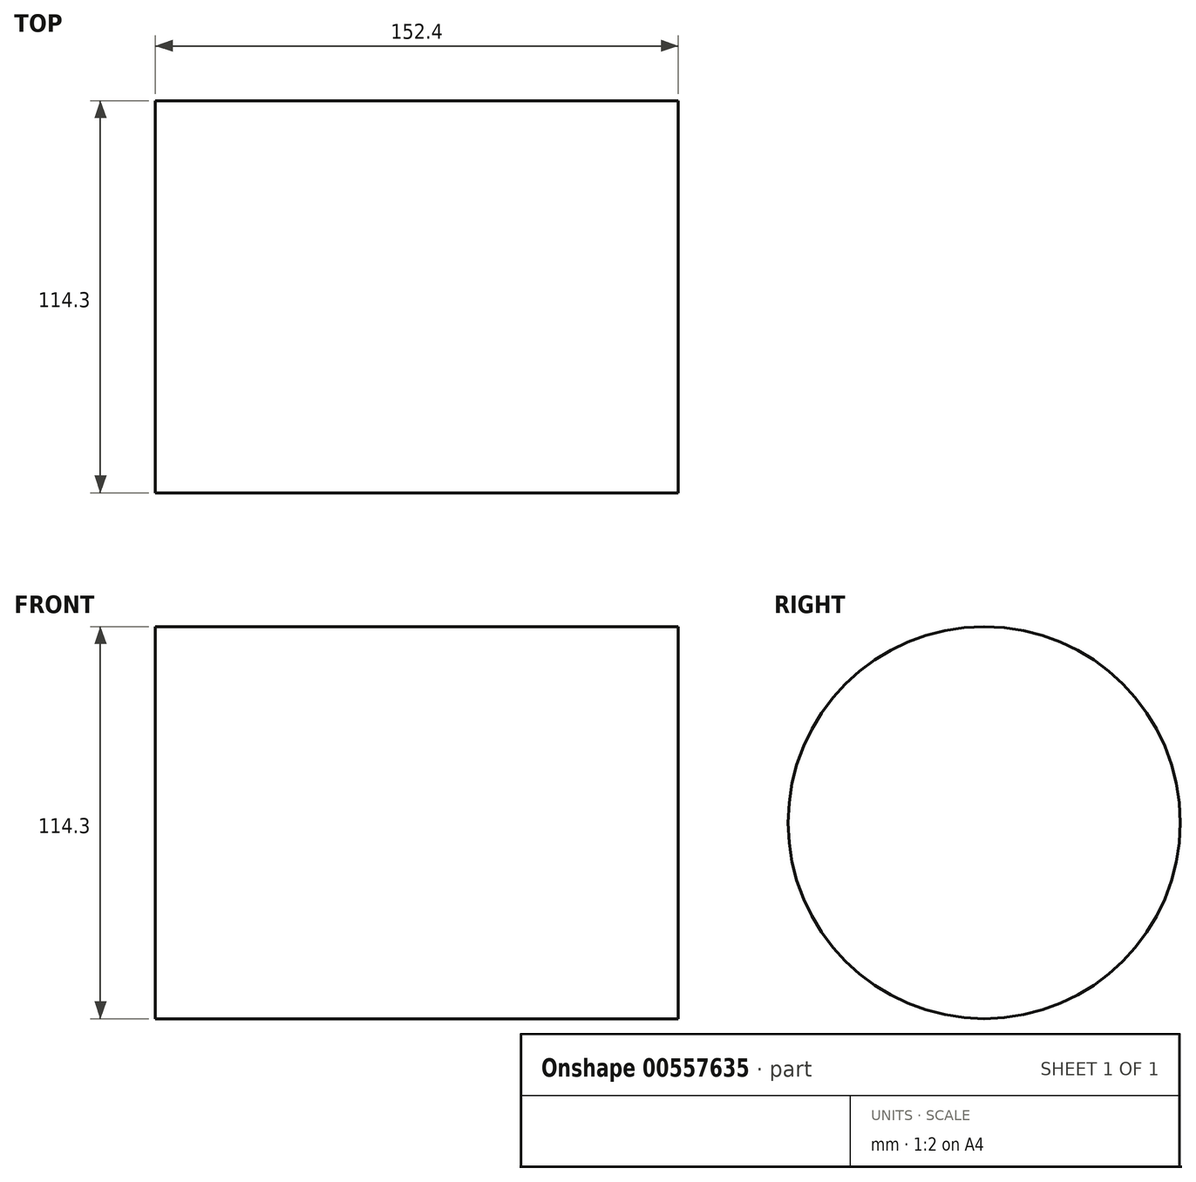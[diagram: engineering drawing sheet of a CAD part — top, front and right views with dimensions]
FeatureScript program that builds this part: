
annotation { "Feature Type Name" : "Feature", "Feature Type Description" : "" }
export const myFeature = defineFeature(function(context is Context, id is Id, definition is map)
    precondition{}
    {
        {
            var Q0;
            Q0=qCreatedBy(makeId("Front.planeOp"),FACE);
            var sketch = newSketch(context, id + "F0", { "sketchPlane" : qUnion([Q0])});
            skLineSegment(sketch, "E0.bottom", {"start": v(-82.1, 57.15) * mm, "end": v(70.3, 57.15) * mm});
            skLineSegment(sketch, "E0.top", {"start": v(-82.1, -57.15) * mm, "end": v(70.3, -57.15) * mm});
            skLineSegment(sketch, "E0.left", {"start": v(-82.1, 57.15) * mm, "end": v(-82.1, -57.15) * mm});
            skLineSegment(sketch, "E0.right", {"start": v(70.3, 57.15) * mm, "end": v(70.3, -57.15) * mm});
            skPoint(sketch, "E0.middle", {"position": v(-5.9, 0) * mm});
            skLineSegment(sketch, "E1.bottom", {"start": v(-82.1, 44.45) * mm, "end": v(-183.7, 44.45) * mm});
            skLineSegment(sketch, "E1.top", {"start": v(-82.1, -44.45) * mm, "end": v(-183.7, -44.45) * mm});
            skLineSegment(sketch, "E1.left", {"start": v(-82.1, 44.45) * mm, "end": v(-82.1, -44.45) * mm});
            skLineSegment(sketch, "E1.right", {"start": v(-183.7, 44.45) * mm, "end": v(-183.7, -44.45) * mm});
            skLineSegment(sketch, "E2", {"start": v(70.3, 0) * mm, "end": v(-82.1, 0) * mm});
            skSolve(sketch);
        }
        {
            var Q0;
            {var subQ5=sQuery(id+"F0.wireOp",EDGE,"E0.bottom");Q0=makeQuery(id+"F0.imprint","IMPRINT",FACE,{"disambiguationData":[TD([[makeQuery(id+"F0.imprint","IMPRINT",EDGE,{"derivedFrom":subQ5}),-1.0]])]});}
            var Q1;
            Q1=sQuery(id+"F0.wireOp",EDGE,"E2");
            revolve(context, id + "F1", {"entities" : qUnion([Q0]), "axis" : qUnion([Q1]), "revolveType" : RevolveType.FULL});
        }
    });
